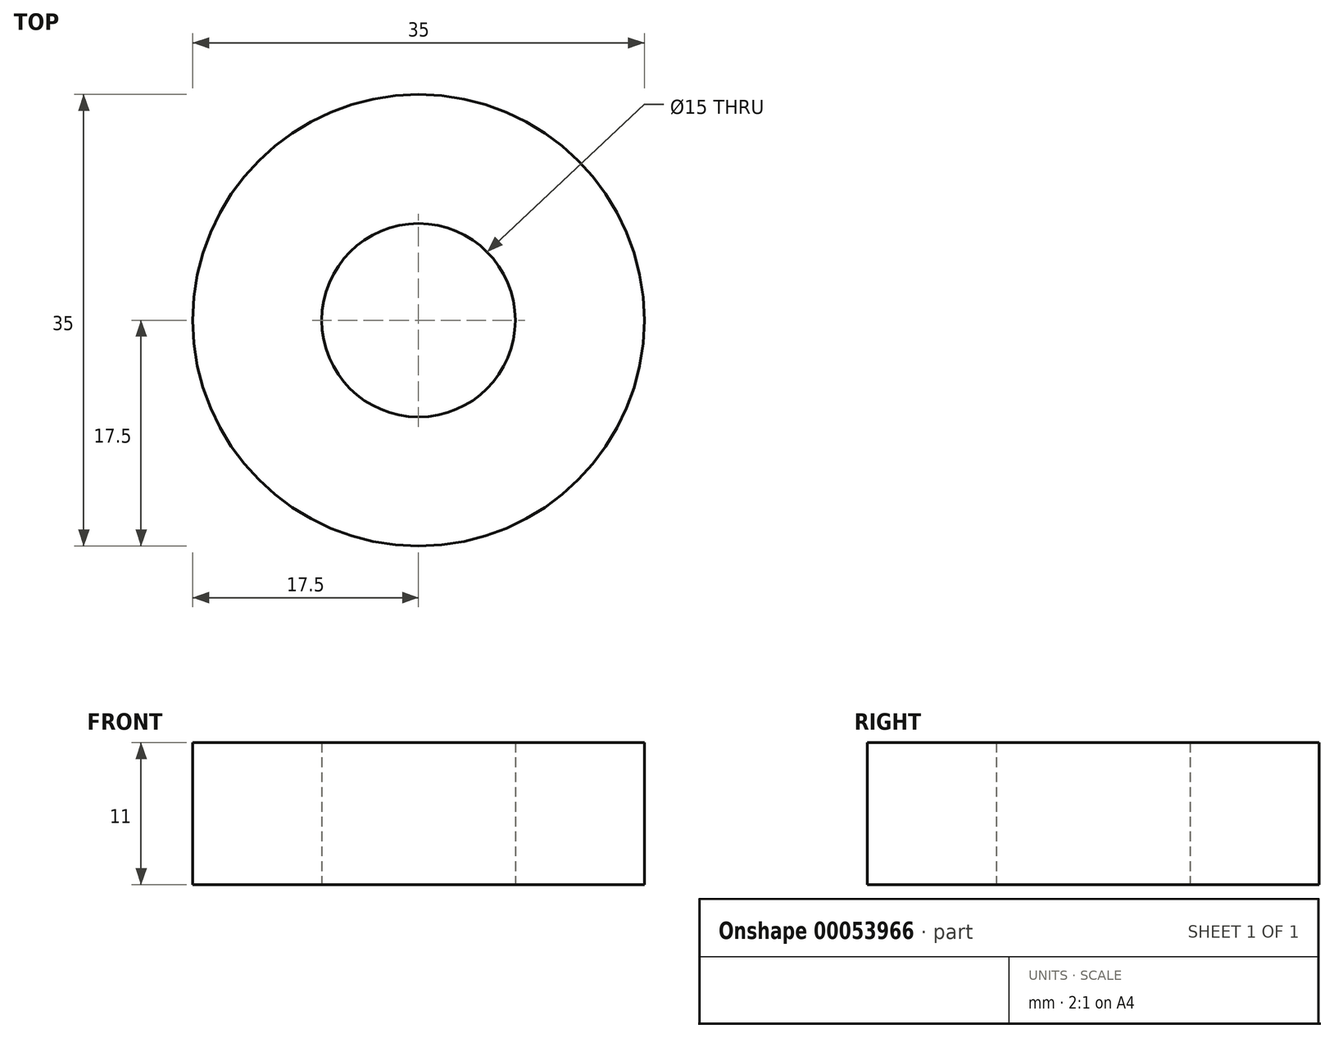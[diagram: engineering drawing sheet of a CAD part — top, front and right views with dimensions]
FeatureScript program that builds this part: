
annotation { "Feature Type Name" : "Feature", "Feature Type Description" : "" }
export const myFeature = defineFeature(function(context is Context, id is Id, definition is map)
    precondition{}
    {
        {
            var Q0;
            Q0=qCreatedBy(makeId("Top.planeOp"),FACE);
            var sketch = newSketch(context, id + "F0", { "sketchPlane" : qUnion([Q0])});
            skCircle(sketch, "E0", {"center": v(0, 0) * mm, "radius": 7.5 * mm});
            skCircle(sketch, "E1", {"center": v(0, 0) * mm, "radius": 17.5 * mm});
            skSolve(sketch);
        }
        {
            var Q0;
            Q0 = qSketchRegion(id + "F0", true);
            extrude(context, id + "F1", {"entities" : qUnion([Q0]), "depth" : 11 * mm});
        }
    });
